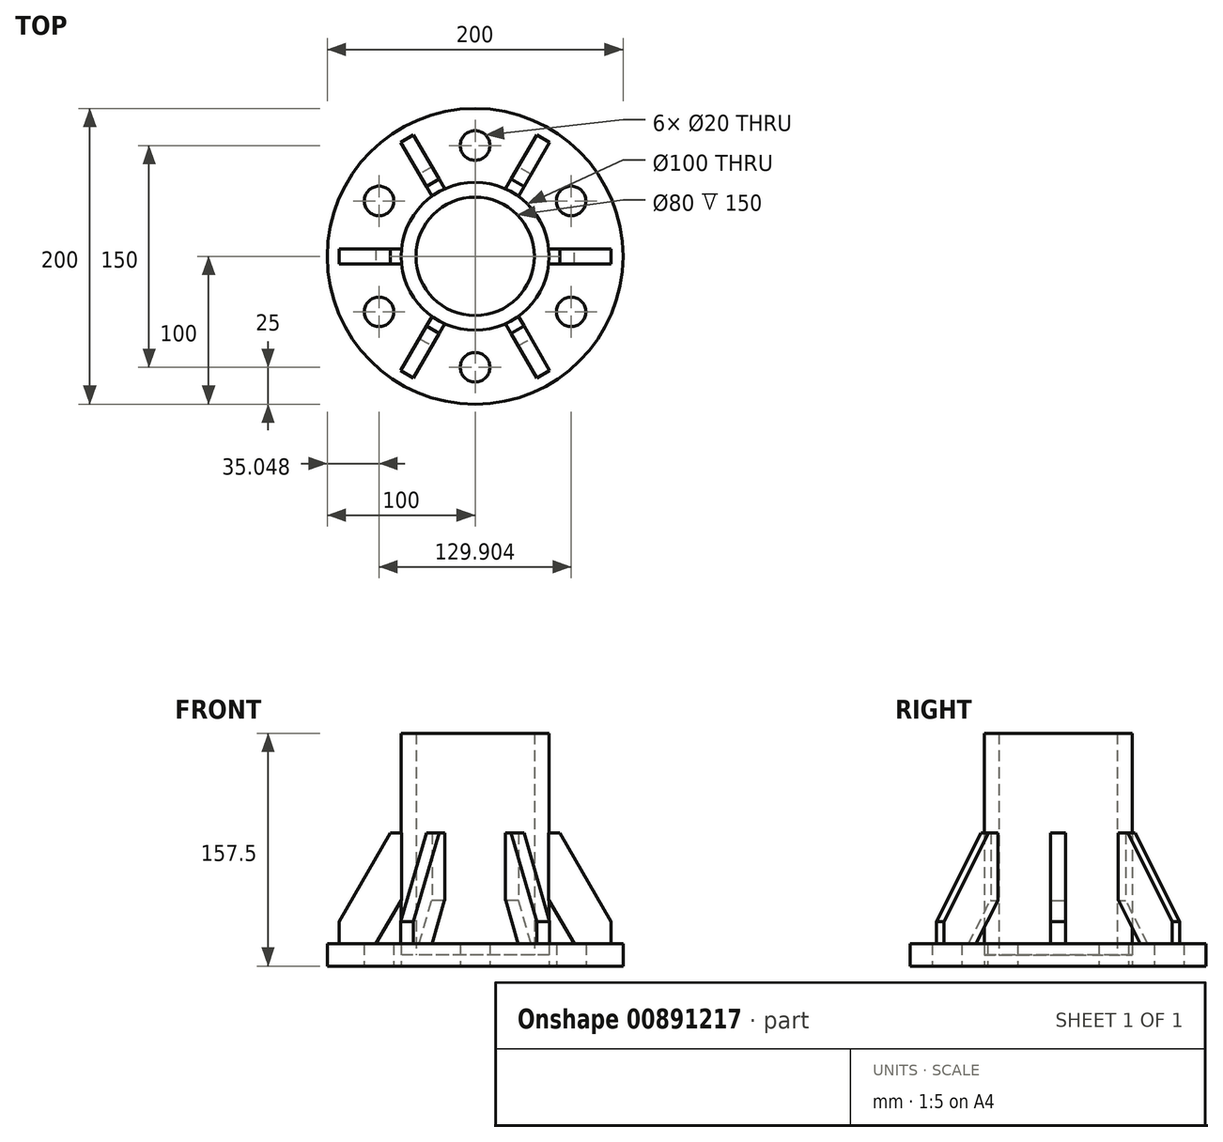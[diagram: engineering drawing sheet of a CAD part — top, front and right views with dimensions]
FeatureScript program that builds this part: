
annotation { "Feature Type Name" : "Feature", "Feature Type Description" : "" }
export const myFeature = defineFeature(function(context is Context, id is Id, definition is map)
    precondition{}
    {
        {
            var Q0;
            Q0=qCreatedBy(makeId("Top.planeOp"),FACE);
            var sketch = newSketch(context, id + "F0", { "sketchPlane" : qUnion([Q0])});
            skCircle(sketch, "E0", {"center": v(0, 0) * mm, "radius": 40 * mm});
            skCircle(sketch, "E1", {"center": v(0, 0) * mm, "radius": 50 * mm});
            skCircle(sketch, "E2", {"center": v(0, 0) * mm, "radius": 100 * mm});
            skCircle(sketch, "E3", {"center": v(0, 0) * mm, "radius": 75 * mm, "construction": true});
            skCircle(sketch, "E4", {"center": v(0, 75) * mm, "radius": 10 * mm});
            skCircle(sketch, "E5.1.0", {"center": v(-64.95, 37.5) * mm, "radius": 10 * mm});
            skCircle(sketch, "E5.2.0", {"center": v(-64.95, -37.5) * mm, "radius": 10 * mm});
            skCircle(sketch, "E5.3.0", {"center": v(0, -75) * mm, "radius": 10 * mm});
            skCircle(sketch, "E5.4.0", {"center": v(64.95, -37.5) * mm, "radius": 10 * mm});
            skCircle(sketch, "E5.5.0", {"center": v(64.95, 37.5) * mm, "radius": 10 * mm});
            skSolve(sketch);
        }
        {
            var Q0;
            Q0=makeQuery(id+"F0.imprint","IMPRINT",FACE,{"disambiguationData":[TD([[makeQuery(id+"F0.imprint","IMPRINT",EDGE,{"derivedFrom":sQuery(id+"F0.wireOp",EDGE,"E0")}),-1.0]])]});
            extrude(context, id + "F1", {"entities" : qUnion([Q0]), "depth" : 157.5 * mm, "offsetDistance" : 25 * mm});
        }
        {
            var Q0;
            Q0=makeQuery(id+"F0.imprint","IMPRINT",FACE,{"disambiguationData":[TD([[makeQuery(id+"F0.imprint","IMPRINT",EDGE,{"derivedFrom":sQuery(id+"F0.wireOp",EDGE,"E1")}),-1.0]])]});
            extrude(context, id + "F2", {"entities" : qUnion([Q0]), "depth" : 15 * mm, "offsetDistance" : 25 * mm});
        }
        {
            var Q0;
            Q0=qCreatedBy(makeId("Front.planeOp"),FACE);
            var sketch = newSketch(context, id + "F3", { "sketchPlane" : qUnion([Q0])});
            skLineSegment(sketch, "E6", {"start": v(0, 0) * mm, "end": v(0, 196.52) * mm, "construction": true});
            skLineSegment(sketch, "E7", {"start": v(100, 0) * mm, "end": v(100, 26.27) * mm, "construction": true});
            skLineSegment(sketch, "E8", {"start": v(0, 0) * mm, "end": v(100, 0) * mm, "construction": true});
            skLineSegment(sketch, "E9", {"start": v(50, 0) * mm, "end": v(50, 157.5) * mm, "construction": true});
            skLineSegment(sketch, "E10", {"start": v(50, 157.5) * mm, "end": v(0, 157.5) * mm, "construction": true});
            skLineSegment(sketch, "E11", {"start": v(50, 90) * mm, "end": v(57.36, 90) * mm});
            skLineSegment(sketch, "E12", {"start": v(57.36, 90) * mm, "end": v(92, 30) * mm});
            skPoint(sketch, "E12.endSnap0", {"position": v(92, 15) * mm});
            skLineSegment(sketch, "E13", {"start": v(92, 30) * mm, "end": v(92, 15) * mm});
            skLineSegment(sketch, "E14", {"start": v(67, 15) * mm, "end": v(50, 44.44) * mm});
            skLineSegment(sketch, "E15", {"start": v(50, 44.44) * mm, "end": v(50, 90) * mm});
            skLineSegment(sketch, "E16", {"start": v(67, 15) * mm, "end": v(92, 15) * mm});
            skLineSegment(sketch, "E17", {"start": v(50, 90) * mm, "end": v(47.4, 90) * mm});
            skLineSegment(sketch, "E18", {"start": v(47.4, 90) * mm, "end": v(47.4, 44.44) * mm});
            skLineSegment(sketch, "E19", {"start": v(47.4, 44.44) * mm, "end": v(50, 44.44) * mm});
            skSolve(sketch);
        }
        {
            var Q0;
            Q0=makeQuery(id+"F3.imprint","IMPRINT",FACE,{"disambiguationData":[TD([[makeQuery(id+"F3.imprint","IMPRINT",EDGE,{"derivedFrom":sQuery(id+"F3.wireOp",EDGE,"E15")}),1.0]])]});
            var Q1;
            Q1=makeQuery(id+"F3.imprint","IMPRINT",FACE,{"disambiguationData":[TD([[makeQuery(id+"F3.imprint","IMPRINT",EDGE,{"derivedFrom":sQuery(id+"F3.wireOp",EDGE,"E11")}),-1.0]])]});
            extrude(context, id + "F4", {"entities" : qUnion([Q0, Q1]), "depth" : 10 * mm, "offsetDistance" : 25 * mm, "symmetric" : true});
        }
        {
            var Q0;
            Q0=makeQuery(id+"F1.opExtrude","SWEPT_BODY",BODY,{"disambiguationData":[OSD([sQuery(id+"F0.wireOp",EDGE,"E0"),sQuery(id+"F0.wireOp",EDGE,"E1")])]});
            var Q1;
            Q1=makeQuery(id+"F4.opExtrude","SWEPT_BODY",BODY,{"disambiguationData":[OSD([sQuery(id+"F3.wireOp",EDGE,"E11"),sQuery(id+"F3.wireOp",EDGE,"E12"),sQuery(id+"F3.wireOp",EDGE,"E13"),sQuery(id+"F3.wireOp",EDGE,"E14"),sQuery(id+"F3.wireOp",EDGE,"E16"),sQuery(id+"F3.wireOp",EDGE,"E17"),sQuery(id+"F3.wireOp",EDGE,"E18"),sQuery(id+"F3.wireOp",EDGE,"E19")])]});
            booleanBodies(context, id + "F5", {"operationType" : BooleanOperationType.SUBTRACTION, "tools" : qUnion([Q0]), "targets" : qUnion([Q1]), "keepTools" : true});
        }
        {
            var Q0;
            Q0=makeQuery(id+"F4.opExtrude","SWEPT_BODY",BODY,{"disambiguationData":[OSD([sQuery(id+"F3.wireOp",EDGE,"E11"),sQuery(id+"F3.wireOp",EDGE,"E12"),sQuery(id+"F3.wireOp",EDGE,"E13"),sQuery(id+"F3.wireOp",EDGE,"E14"),sQuery(id+"F3.wireOp",EDGE,"E16"),sQuery(id+"F3.wireOp",EDGE,"E17"),sQuery(id+"F3.wireOp",EDGE,"E18"),sQuery(id+"F3.wireOp",EDGE,"E19")])]});
            var Q1;
            Q1=sQuery(id+"F3.wireOp",EDGE,"E6");
            circularPattern(context, id + "F6", {"entities" : qUnion([Q0]), "axis" : qUnion([Q1]), "angle" : 360 * degree, "instanceCount" : 6, "equalSpace" : true});
        }
        {
            var Q0;
            Q0=makeQuery(id+"F0.imprint","IMPRINT",FACE,{"disambiguationData":[TD([[makeQuery(id+"F0.imprint","IMPRINT",EDGE,{"derivedFrom":sQuery(id+"F0.wireOp",EDGE,"E0")}),1.0]])]});
            extrude(context, id + "F7", {"entities" : qUnion([Q0]), "operationType" : NewBodyOperationType.ADD, "depth" : 7.5 * mm, "offsetDistance" : 25 * mm});
        }
        {
            var Q0;
            Q0=makeQuery(id+"F0.imprint","IMPRINT",FACE,{"disambiguationData":[TD([[makeQuery(id+"F0.imprint","IMPRINT",EDGE,{"derivedFrom":sQuery(id+"F0.wireOp",EDGE,"E0")}),1.0]])]});
            extrude(context, id + "F8", {"entities" : qUnion([Q0]), "operationType" : NewBodyOperationType.REMOVE, "depth" : 7.5 * mm, "offsetDistance" : 25 * mm});
        }
        {
            var Q0;
            Q0=makeQuery(id+"F0.imprint","IMPRINT",FACE,{"disambiguationData":[TD([[makeQuery(id+"F0.imprint","IMPRINT",EDGE,{"derivedFrom":sQuery(id+"F0.wireOp",EDGE,"E0")}),-1.0]])]});
            extrude(context, id + "F9", {"entities" : qUnion([Q0]), "operationType" : NewBodyOperationType.REMOVE, "depth" : 7.5 * mm, "offsetDistance" : 25 * mm});
        }
    });
